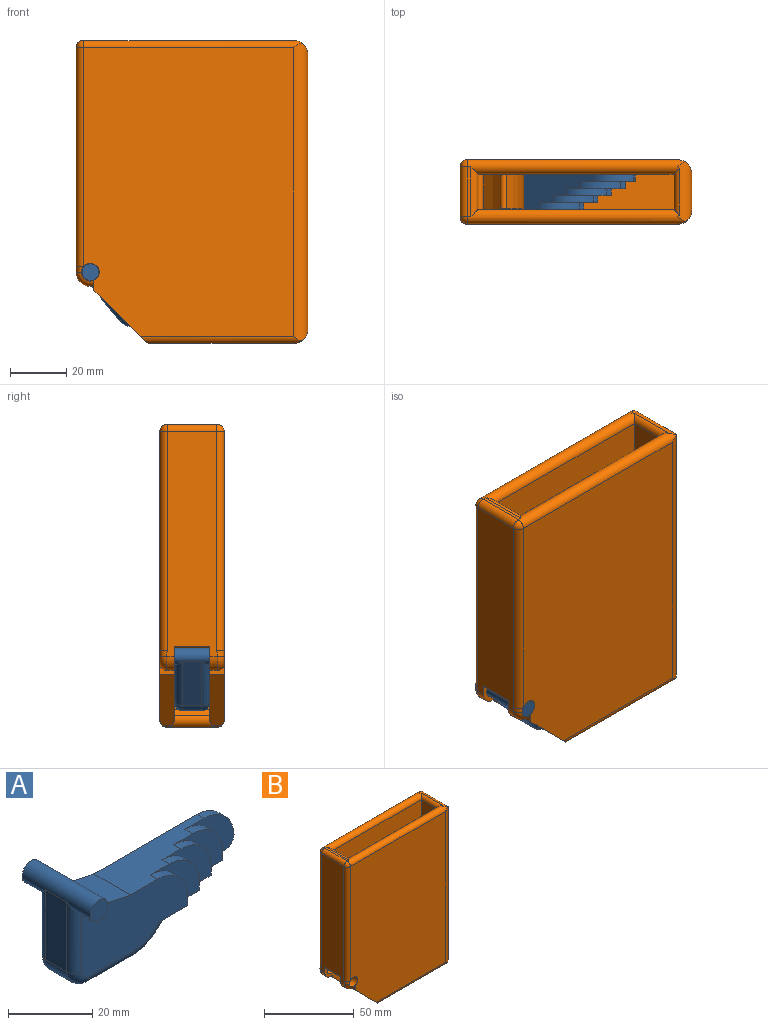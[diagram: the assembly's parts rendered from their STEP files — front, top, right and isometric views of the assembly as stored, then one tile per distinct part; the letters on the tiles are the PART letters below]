
ASSEMBLY  parts=2 mates=1
PART A: 37 faces, bbox 63.9x22.9x29.4 mm
  f0: cylinder r=2.98mm len=22.86mm, axis (0,1,0), area 379.5mm2, adj f1,f2,f3,f11,f12,f13,f27,f32
  f1: plane 5.97x5.97mm, normal (0,-1,0), area 28mm2, adj f0
  f2: plane 5.97x5.97mm, normal (0,1,0), area 28mm2, adj f0
  f3: plane 20.32x7.11mm, normal (-1,0,0), area 144.5mm2, adj f0,f26,f27,f32
  f4: plane 15.06x7.11mm, normal (0,0,-1), area 107.1mm2, adj f5,f26,f29,f34
  f5: cylinder r=12.7mm len=8.98mm, axis (0,1,0), area 70.9mm2, adj f4,f6,f30,f35
  f6: plane 7.11x2.88mm, normal (0.71,0,-0.71), area 29mm2, adj f5,f7,f31,f36
  f7: plane 31.91x12.19mm, normal (0,0,-1), area 224.9mm2, adj f6,f8,f12,f13,f14,f16,f17,f19
  f8: plane 2.54x2.44mm, normal (1,0,0), area 6.2mm2, adj f7,f9,f12,f16
  f9: cylinder r=10.16mm len=10.16mm, axis (0,1,0), area 38.9mm2, adj f8,f10,f12,f16
  f10: plane 34.54x12.19mm, normal (0,0,1), area 265.4mm2, adj f9,f11,f12,f13,f15,f16,f18,f19
  f11: plane 15.81x12.19mm, normal (0.19,0,0.98), area 196.5mm2, adj f0,f10,f12,f13
  f12: plane 35.56x19.91mm, normal (0,-1,0), area 548.7mm2, adj f0,f7,f8,f9,f10,f11,f32,f33
  f13: plane 60.95x19.91mm, normal (0,1,0), area 869.1mm2, adj f0,f7,f10,f11,f23,f24,f27,f28
  f14: plane 2.54x2.44mm, normal (1,0,0), area 6.2mm2, adj f7,f15,f16,f19
  f15: cylinder r=10.16mm len=10.16mm, axis (0,1,0), area 38.9mm2, adj f10,f14,f16,f19
  f16: plane 16.51x12.7mm, normal (0,-1,0), area 80.6mm2, adj f7,f8,f9,f10,f14,f15
  f17: plane 2.54x2.44mm, normal (1,0,0), area 6.2mm2, adj f7,f18,f19,f22
  f18: cylinder r=10.16mm len=10.16mm, axis (0,1,0), area 38.9mm2, adj f10,f17,f19,f22
  f19: plane 16.51x12.7mm, normal (0,-1,0), area 80.6mm2, adj f7,f10,f14,f15,f17,f18
  f20: plane 2.59x2.54mm, normal (1,0,0), area 6.6mm2, adj f7,f21,f22,f25
  f21: cylinder r=10.16mm len=10.16mm, axis (0,-1,0), area 41.3mm2, adj f10,f20,f22,f25
  f22: plane 16.51x12.7mm, normal (0,-1,0), area 80.6mm2, adj f7,f10,f17,f18,f20,f21
  f23: cylinder r=10.16mm len=10.15mm, axis (0,-1,0), area 35.6mm2, adj f10,f13,f24,f25
  f24: cylinder r=3.17mm len=3.17mm, axis (0,-1,0), area 10.9mm2, adj f7,f13,f23,f25
  f25: plane 16.5x12.7mm, normal (0,-1,0), area 78.5mm2, adj f7,f10,f20,f21,f23,f24
  f26: cylinder r=5.08mm len=7.11mm, axis (0,1,0), area 56.8mm2, adj f3,f4,f28,f33
  f27: cylinder r=2.54mm len=20.32mm, axis (0,0,-1), area 73.9mm2, adj f0,f3,f13,f28
  f28: torus R=2.54mm, axis (0,-1,0), area 26.1mm2, adj f13,f26,f27,f29
  f29: cylinder r=2.54mm len=15.06mm, axis (1,0,0), area 60.1mm2, adj f4,f13,f28,f30
  f30: torus R=10.16mm, axis (0,-1,0), area 36.9mm2, adj f5,f13,f29,f31
  f31: cylinder r=2.54mm len=4.68mm, axis (0.71,0,0.71), area 12.6mm2, adj f6,f7,f13,f30
  f32: cylinder r=2.54mm len=20.32mm, axis (0,0,1), area 73.9mm2, adj f0,f3,f12,f33
  f33: torus R=2.54mm, axis (0,-1,0), area 26.1mm2, adj f12,f26,f32,f34
  f34: cylinder r=2.54mm len=15.06mm, axis (-1,0,0), area 60.1mm2, adj f4,f12,f33,f35
  f35: torus R=10.16mm, axis (0,-1,0), area 36.9mm2, adj f5,f12,f34,f36
  f36: cylinder r=2.54mm len=4.68mm, axis (-0.71,0,-0.71), area 12.6mm2, adj f6,f7,f12,f35
PART B: 53 faces, bbox 83.4x23.5x108.4 mm
  f0: plane 18.46x18.46mm, normal (-0.71,0,-0.71), area 130.3mm2, adj f2,f11,f15,f38,f39
  f1: cylinder r=5.08mm len=6.35mm, axis (0,1,0), area 24.3mm2, adj f2,f4,f15,f37
  f2: plane 5.52x3.88mm, normal (-1,0,0), area 8.5mm2, adj f0,f1,f11,f15,f37
  f3: plane 17.78x1.27mm, normal (0,0,1), area 22.6mm2, adj f26,f29,f31,f33
  f4: plane 80.01x17.94mm, normal (-1,0,0), area 1377.1mm2, adj f1,f5,f15,f16,f27,f30,f33,f35
  f5: cylinder r=5.08mm len=6.35mm, axis (0,1,0), area 24.3mm2, adj f4,f6,f16,f25
  f6: plane 5.52x3.88mm, normal (-1,0,0), area 8.5mm2, adj f5,f7,f10,f16,f25
  f7: plane 18.46x18.46mm, normal (-0.71,0,-0.71), area 130.3mm2, adj f6,f10,f16,f41,f42
  f8: plane 41.63x17.78mm, normal (0,0,-1), area 740.1mm2, adj f24,f38,f40,f41
  f9: plane 97.79x12.7mm, normal (1,0,0), area 1241.9mm2, adj f21,f22,f23,f24
  f10: plane 102.87x74.93mm, normal (0,-1,0), area 7465.7mm2, adj f6,f7,f18,f22,f26,f30,f41
  f11: plane 102.87x74.93mm, normal (0,1,0), area 7465.7mm2, adj f0,f2,f19,f23,f31,f35,f38
  f12: plane 99.06x12.7mm, normal (-1,0,0), area 1258.1mm2, adj f14,f15,f16,f28
  f13: plane 75.09x12.7mm, normal (1,0,0), area 850.6mm2, adj f15,f16,f17,f29,f46,f47,f48,f49
  f14: plane 40.14x12.7mm, normal (0,0,1), area 509.8mm2, adj f12,f15,f16,f20
  f15: plane 102.87x76.2mm, normal (0,-1,0), area 6912.3mm2, adj f0,f1,f2,f4,f12,f13,f14,f17
  f16: plane 102.87x76.2mm, normal (0,1,0), area 6912.3mm2, adj f4,f5,f6,f7,f12,f13,f14,f17
  f17: cylinder r=5.08mm len=12.7mm, axis (0,-1,0), area 73.8mm2, adj f13,f15,f16,f43
  f18: cylinder r=3.17mm len=6.35mm, axis (0,1,0), area 101.3mm2, adj f10,f16,f25,f27
  f19: cylinder r=3.17mm len=6.35mm, axis (0,1,0), area 101.3mm2, adj f11,f15,f36,f37
  f20: plane 12.7x2.01mm, normal (-0.71,0,0.71), area 36.2mm2, adj f14,f15,f16,f40
  f21: cylinder r=5.08mm len=21.37mm, axis (0,1,0), area 132.3mm2, adj f9,f22,f23,f26,f28,f31
  f22: cylinder r=5.08mm len=106.46mm, axis (0,0,-1), area 824.2mm2, adj f9,f10,f21,f24,f26,f41
  f23: cylinder r=5.08mm len=106.46mm, axis (0,0,1), area 824.2mm2, adj f9,f11,f21,f24,f31,f38
  f24: cylinder r=5.08mm len=21.37mm, axis (0,1,0), area 145.2mm2, adj f8,f9,f22,f23,f38,f41
  f25: torus R=2.54mm, axis (0,-1,0), area 28mm2, adj f5,f6,f18,f27
  f26: cylinder r=2.54mm len=77.58mm, axis (1,0,0), area 590mm2, adj f3,f10,f16,f21,f22,f28,f29,f32
  f27: bspline ~2.63x2.61mm, area 6.8mm2, adj f4,f18,f25,f30
  f28: cylinder r=2.54mm len=16.73mm, axis (0,-1,0), area 48.9mm2, adj f12,f21,f26,f31
  f29: cylinder r=2.54mm len=17.78mm, axis (0,1,0), area 58mm2, adj f3,f13,f26,f31
  f30: cylinder r=2.54mm len=78.11mm, axis (0,0,1), area 311.6mm2, adj f4,f10,f27,f32
  f31: cylinder r=2.54mm len=77.58mm, axis (-1,0,0), area 590mm2, adj f3,f11,f15,f21,f23,f28,f29,f34
  f32: sphere r=2.54mm, area 10.1mm2, adj f26,f30,f33
  f33: cylinder r=2.54mm len=17.78mm, axis (0,-1,0), area 70.9mm2, adj f3,f4,f32,f34
  f34: sphere r=2.54mm, area 10.1mm2, adj f31,f33,f35
  f35: cylinder r=2.54mm len=78.11mm, axis (0,0,-1), area 311.6mm2, adj f4,f11,f34,f36
  f36: bspline ~2.63x2.61mm, area 6.8mm2, adj f4,f19,f35,f37
  f37: torus R=2.54mm, axis (0,1,0), area 28mm2, adj f1,f2,f19,f36
  f38: cylinder r=2.54mm len=57.26mm, axis (1,0,0), area 254.2mm2, adj f0,f8,f11,f15,f23,f24,f39,f40
  f39: cylinder r=2.54mm len=3.59mm, axis (0,1,0), area 3.6mm2, adj f0,f38
  f40: cylinder r=2.54mm len=17.78mm, axis (0,1,0), area 83.4mm2, adj f8,f15,f16,f20,f38,f41
  f41: cylinder r=2.54mm len=57.26mm, axis (1,0,0), area 254.2mm2, adj f7,f8,f10,f16,f22,f24,f40,f42
  f42: cylinder r=2.54mm len=3.59mm, axis (0,1,0), area 3.6mm2, adj f7,f41
  f43: cylinder r=0.64mm len=12.7mm, axis (0,-1,0), area 19.9mm2, adj f4,f15,f16,f17
  f44: cylinder r=36.4mm len=46.29mm, axis (0,1,0), area 616.4mm2, adj f46,f47,f49,f50,f51,f52
  f45: cylinder r=38.94mm len=51.23mm, axis (0,1,0), area 692.5mm2, adj f46,f47,f48,f50
  f46: plane 55.76x16.33mm, normal (0,-1,0), area 145.2mm2, adj f13,f44,f45,f48,f49,f50,f51
  f47: plane 55.76x16.33mm, normal (0,1,0), area 145.2mm2, adj f13,f44,f45,f48,f49,f50,f52
  f48: cylinder r=5.08mm len=12.19mm, axis (0,1,0), area 55.2mm2, adj f13,f45,f46,f47
  f49: cylinder r=1.27mm len=12.19mm, axis (0,1,0), area 35.9mm2, adj f13,f44,f46,f47
  f50: cylinder r=1.27mm len=12.19mm, axis (0,1,0), area 45.5mm2, adj f44,f45,f46,f47,f51,f52
  f51: cylinder r=1.27mm len=3.74mm, axis (0,0,1), area 3.9mm2, adj f44,f46,f50
  f52: cylinder r=1.27mm len=3.74mm, axis (0,0,-1), area 3.9mm2, adj f44,f47,f50
PLACE A rot(axis=(0,-1,0),39.6deg) t=(-61.63,-37.04,-16.69)mm
PLACE B t=(-17.56,-37.04,23.06)mm fixed
MATE revolute A.f0 <-> B.f1  axis (0,1,0) through (-61.63,-25.61,-16.69)mm
